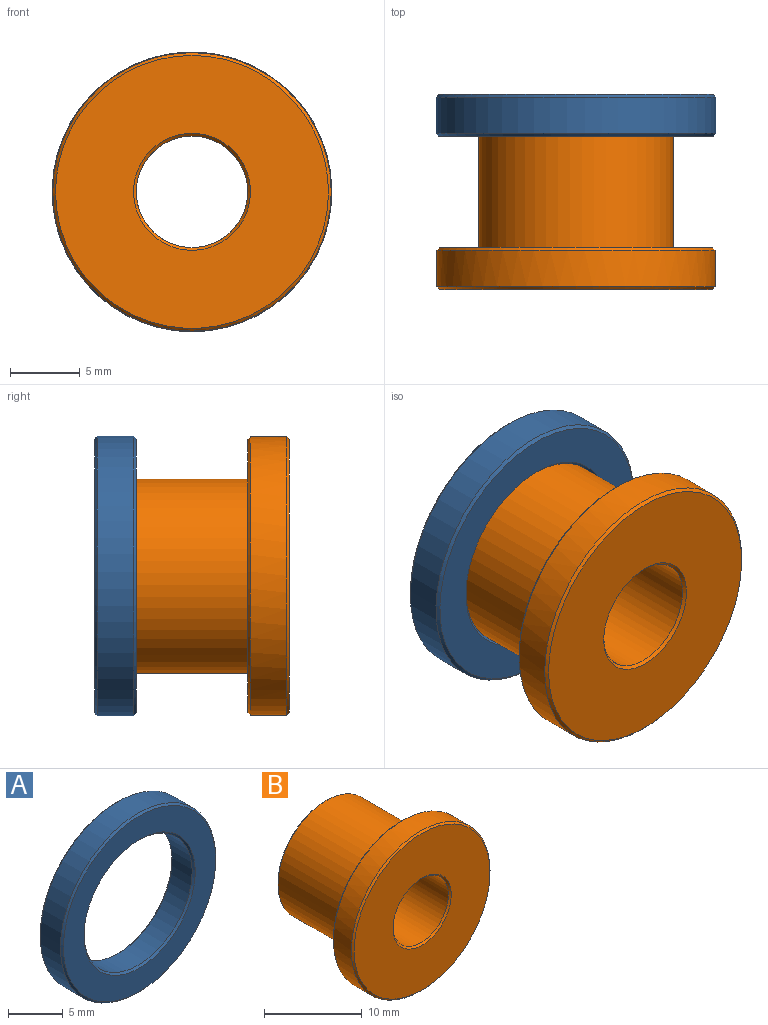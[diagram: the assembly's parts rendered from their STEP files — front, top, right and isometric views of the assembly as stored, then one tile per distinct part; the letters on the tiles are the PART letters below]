
ASSEMBLY  parts=2 mates=1
PART A: 8 faces, bbox 20.1x3x20.1 mm
  f0: plane 19.7x19.7mm, normal (0,-1,0), area 141.9mm2, adj f5,f7
  f1: cylinder r=7mm len=14mm, axis (0,-1,0), area 114.4mm2, adj f4,f5
  f2: plane 19.7x19.7mm, normal (0,1,0), area 141.9mm2, adj f4,f6
  f3: cylinder r=10.05mm len=20.1mm, axis (0,-1,0), area 164.2mm2, adj f6,f7
  f4: cone r=7.2mm half-angle=45deg, axis (0,1,0), area 12.6mm2, adj f1,f2
  f5: cone r=7mm half-angle=45deg, axis (0,-1,0), area 12.6mm2, adj f0,f1
  f6: cone r=10.05mm half-angle=45deg, axis (0,-1,0), area 17.7mm2, adj f2,f3
  f7: cone r=9.85mm half-angle=45deg, axis (0,1,0), area 17.7mm2, adj f0,f3
PART B: 11 faces, bbox 20x14x20 mm
  f0: plane 19.6x19.6mm, normal (0,-1,0), area 246.3mm2, adj f6,f10
  f1: cylinder r=4mm len=13.6mm, axis (0,-1,0), area 341.8mm2, adj f6,f7
  f2: plane 13.6x13.6mm, normal (0,1,0), area 89.8mm2, adj f7,f8
  f3: cylinder r=7mm len=14mm, axis (0,-1,0), area 475mm2, adj f4,f8
  f4: plane 19.6x19.6mm, normal (0,1,0), area 147.8mm2, adj f3,f9
  f5: cylinder r=10mm len=20mm, axis (0,-1,0), area 163.4mm2, adj f9,f10
  f6: cone r=4mm half-angle=45deg, axis (0,-1,0), area 7.3mm2, adj f0,f1
  f7: cone r=4.2mm half-angle=45deg, axis (0,1,0), area 7.3mm2, adj f1,f2
  f8: cone r=7mm half-angle=45deg, axis (0,-1,0), area 12.3mm2, adj f2,f3
  f9: cone r=10mm half-angle=45deg, axis (0,-1,0), area 17.6mm2, adj f4,f5
  f10: cone r=9.8mm half-angle=45deg, axis (0,1,0), area 17.6mm2, adj f0,f5
PLACE A t=(2.79,7.91,3.44)mm
PLACE B t=(2.79,-3.09,3.44)mm
MATE cylindrical A.f1 <-> B.f1  axis (0,-1,0) through (2.79,10.71,3.44)mm
